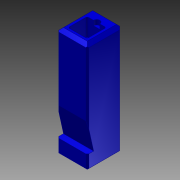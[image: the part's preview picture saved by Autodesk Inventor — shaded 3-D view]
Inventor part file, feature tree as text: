
AUTODESK INVENTOR PART (.ipt)
format: ipt  version: 2012 (Build 160160000, 160)  size: 211,968 bytes
history: native  units: mm
features: fillet x5, extrude x4, chamfer x4, sketch x1, revolve x1
ambient origin geometry x8: Origin, YZ Plane, XZ Plane, XY Plane, X Axis, Y Axis, Z Axis, Center Point
bodies: Solid1 (feature_tree)
feature tree (15):
  sketch  "Sketch2"  dims[d1=70.0mm d2=13.0mm d3=8.2mm d4=32.0mm d5=4.0mm d6=60.0mm d7=18.0mm d8=19.0mm d9=0.0mm d10=12.0mm d11=11.0mm d12=6.0mm d13=12.0mm d14=0.0mm d15=1.0mm d16=9.4mm d17=2.0mm d18=2.0mm d19=45.0deg d20=2.0mm d21=2.0mm d22=45.0deg d23=2.0mm d24=2.0mm d25=45.0deg d28=8.0mm d30=6.0mm d31=12.0mm d32=0.0mm d33=6.0mm d34=0.0mm d35=2.0mm d36=1.0mm d37=1.0mm d38=1.0mm d39=1.0mm d40=2.0mm d41=45.0deg d42=4.0mm d43=7.0mm d44=5.0mm d45=4.0mm d46=2.0mm d47=3.0mm d48=90.0deg]
  extrude  "Extrusion1"  Depth=13.0mm
  extrude  "Extrusion2"  Depth=8.2mm
  fillet  "Fillet1"  Radius=32.0mm
  chamfer  "Chamfer1"  Distance=4.0mm
  chamfer  "Chamfer2"  Distance=60.0mm
  chamfer  "Chamfer3"  Distance=18.0mm
  extrude  "Extrusion3"  Depth=19.0mm TaperAngle=0.0deg
  extrude  "Extrusion4"  Depth=12.0mm
  fillet  "Fillet2"  Radius=11.0mm
  fillet  "Fillet3"  Radius=6.0mm
  fillet  "Fillet4"  Radius=12.0mm
  fillet  "Fillet5"  Radius=1.0mm
  chamfer  "Chamfer4"  Distance=9.4mm
  revolve  "Revolution1"  Angle=45.0deg
